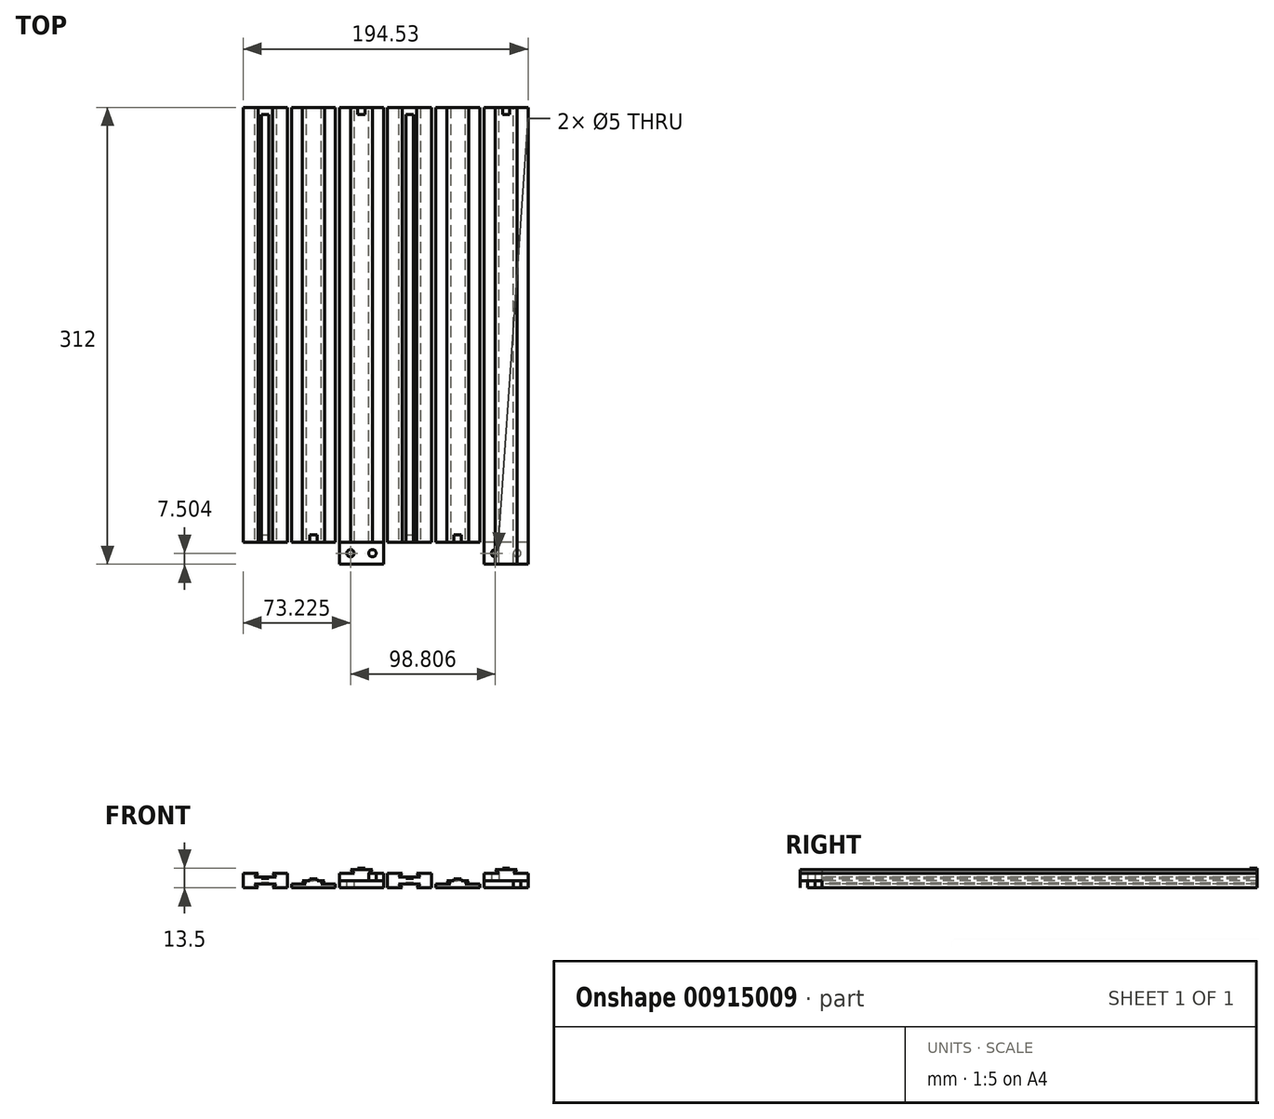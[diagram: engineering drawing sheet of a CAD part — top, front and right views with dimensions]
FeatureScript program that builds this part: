
annotation { "Feature Type Name" : "Feature", "Feature Type Description" : "" }
export const myFeature = defineFeature(function(context is Context, id is Id, definition is map)
    precondition{}
    {
        {
            var Q0;
            Q0=qCreatedBy(makeId("Top.planeOp"),FACE);
            var sketch = newSketch(context, id + "F0", { "sketchPlane" : qUnion([Q0])});
            skLineSegment(sketch, "E0.bottom", {"start": v(15, 5) * mm, "end": v(-15, 5) * mm});
            skLineSegment(sketch, "E0.top", {"start": v(15, -5) * mm, "end": v(-15, -5) * mm});
            skLineSegment(sketch, "E0.left", {"start": v(15, 5) * mm, "end": v(15, -5) * mm});
            skLineSegment(sketch, "E0.right", {"start": v(-15, 5) * mm, "end": v(-15, -5) * mm});
            skPoint(sketch, "E0.middle", {"position": v(0, 0) * mm});
            skSolve(sketch);
        }
        {
            var Q0;
            Q0 = qSketchRegion(id + "F0", true);
            extrude(context, id + "F1", {"entities" : qUnion([Q0]), "depth" : 297 * mm, "offsetDistance" : 25.4 * mm});
        }
        {
            var Q0;
            Q0=makeQuery(id+"F1.opExtrude","CAP_FACE",FACE,{"disambiguationData":[OSD([sQuery(id+"F0.wireOp",EDGE,"E0.bottom"),sQuery(id+"F0.wireOp",EDGE,"E0.top"),sQuery(id+"F0.wireOp",EDGE,"E0.left"),sQuery(id+"F0.wireOp",EDGE,"E0.right")])],"isStart":false});
            var sketch = newSketch(context, id + "F2", { "sketchPlane" : qUnion([Q0])});
            skLineSegment(sketch, "E1", {"start": v(5, -5) * mm, "end": v(7.5, -2.5) * mm});
            skLineSegment(sketch, "E2", {"start": v(7.5, -2.5) * mm, "end": v(-7.5, -2.5) * mm});
            skLineSegment(sketch, "E3", {"start": v(-7.5, -2.5) * mm, "end": v(-5, -5) * mm});
            skLineSegment(sketch, "E4", {"start": v(-5, -5) * mm, "end": v(5, -5) * mm});
            skLineSegment(sketch, "E5", {"start": v(0, 5) * mm, "end": v(0, -5) * mm, "construction": true});
            skLineSegment(sketch, "E6", {"start": v(0, -5) * mm, "end": v(0, -2.5) * mm, "construction": true});
            skLineSegment(sketch, "E7", {"start": v(7.5, 2.5) * mm, "end": v(-7.5, 2.5) * mm});
            skLineSegment(sketch, "E8.MirrorCS", {"start": v(-5, 5) * mm, "end": v(5, 5) * mm});
            skLineSegment(sketch, "E9.MirrorCS", {"start": v(-7.5, 2.5) * mm, "end": v(-5, 5) * mm});
            skLineSegment(sketch, "E10.MirrorCS", {"start": v(5, 5) * mm, "end": v(7.5, 2.5) * mm});
            skSolve(sketch);
        }
        {
            var Q0;
            Q0=makeQuery(id+"F2.imprint","IMPRINT",FACE,{"disambiguationData":[TD([[makeQuery(id+"F2.imprint","IMPRINT",EDGE,{"derivedFrom":sQuery(id+"F2.wireOp",EDGE,"E7")}),-1.0]])]});
            var Q1;
            Q1=makeQuery(id+"F2.imprint","IMPRINT",FACE,{"disambiguationData":[TD([[makeQuery(id+"F2.imprint","IMPRINT",EDGE,{"derivedFrom":sQuery(id+"F2.wireOp",EDGE,"E1")}),1.0]])]});
            extrude(context, id + "F3", {"entities" : qUnion([Q0, Q1]), "operationType" : NewBodyOperationType.REMOVE, "oppositeDirection" : true, "depth" : 297 * mm, "offsetDistance" : 25.4 * mm});
        }
        {
            var Q0;
            Q0=qCreatedBy(makeId("Top.planeOp"),FACE);
            var sketch = newSketch(context, id + "F4", { "sketchPlane" : qUnion([Q0])});
            skLineSegment(sketch, "E11.bottom", {"start": v(17.89, 5) * mm, "end": v(47.89, 5) * mm});
            skLineSegment(sketch, "E11.top", {"start": v(17.89, 0) * mm, "end": v(47.89, 0) * mm});
            skLineSegment(sketch, "E11.left", {"start": v(17.89, 5) * mm, "end": v(17.89, 0) * mm});
            skLineSegment(sketch, "E11.right", {"start": v(47.89, 5) * mm, "end": v(47.89, 0) * mm});
            skLineSegment(sketch, "E12", {"start": v(0, 0) * mm, "end": v(22.12, 0) * mm, "construction": true});
            skLineSegment(sketch, "E13", {"start": v(32.89, 5) * mm, "end": v(32.89, 0) * mm, "construction": true});
            skLineSegment(sketch, "E14", {"start": v(37.89, 2.5) * mm, "end": v(40.39, 5) * mm});
            skLineSegment(sketch, "E15", {"start": v(40.39, 5) * mm, "end": v(25.39, 5) * mm});
            skLineSegment(sketch, "E16", {"start": v(25.39, 5) * mm, "end": v(27.89, 2.5) * mm});
            skLineSegment(sketch, "E17", {"start": v(27.89, 2.5) * mm, "end": v(37.89, 2.5) * mm});
            skLineSegment(sketch, "E18", {"start": v(32.89, 2.5) * mm, "end": v(32.89, 5) * mm, "construction": true});
            skLineSegment(sketch, "E19", {"start": v(27.89, 2.5) * mm, "end": v(17.89, 2.5) * mm});
            skLineSegment(sketch, "E20", {"start": v(17.89, 2.5) * mm, "end": v(17.89, 5) * mm});
            skLineSegment(sketch, "E21", {"start": v(37.89, 2.5) * mm, "end": v(47.89, 2.5) * mm});
            skLineSegment(sketch, "E22", {"start": v(47.89, 2.5) * mm, "end": v(47.89, 5) * mm});
            skSolve(sketch);
        }
        {
            var Q0;
            Q0=makeQuery(id+"F4.imprint","IMPRINT",FACE,{"disambiguationData":[TD([[makeQuery(id+"F4.imprint","IMPRINT",EDGE,{"derivedFrom":sQuery(id+"F4.wireOp",EDGE,"E14")}),1.0]])]});
            var Q1;
            Q1=makeQuery(id+"F4.imprint","IMPRINT",FACE,{"disambiguationData":[TD([[makeQuery(id+"F4.imprint","IMPRINT",EDGE,{"derivedFrom":sQuery(id+"F4.wireOp",EDGE,"E11.top")}),1.0]])]});
            var Q2;
            {var subQ2=sQuery(id+"F4.wireOp",EDGE,"E16");Q2=makeQuery(id+"F4.imprint","IMPRINT",FACE,{"disambiguationData":[TD([[makeQuery(id+"F4.imprint","IMPRINT",EDGE,{"derivedFrom":subQ2}),-1.0]])]});}
            var Q3;
            {var subQ2=sQuery(id+"F4.wireOp",EDGE,"E14");Q3=makeQuery(id+"F4.imprint","IMPRINT",FACE,{"disambiguationData":[TD([[makeQuery(id+"F4.imprint","IMPRINT",EDGE,{"derivedFrom":subQ2}),-1.0]])]});}
            extrude(context, id + "F5", {"entities" : qUnion([Q0, Q1, Q2, Q3]), "depth" : 297 * mm, "offsetDistance" : 25.4 * mm});
        }
        {
            var Q0;
            Q0=makeQuery(id+"F5.opExtrude","CAP_FACE",FACE,{"disambiguationData":[OSD([sQuery(id+"F4.wireOp",EDGE,"E11.bottom"),sQuery(id+"F4.wireOp",EDGE,"E11.top"),sQuery(id+"F4.wireOp",EDGE,"E11.left"),sQuery(id+"F4.wireOp",EDGE,"E11.right"),sQuery(id+"F4.wireOp",EDGE,"E15"),sQuery(id+"F4.wireOp",EDGE,"E20"),sQuery(id+"F4.wireOp",EDGE,"E22")])],"isStart":false});
            var sketch = newSketch(context, id + "F6", { "sketchPlane" : qUnion([Q0])});
            skLineSegment(sketch, "E23", {"start": v(37.89, 2.5) * mm, "end": v(40.39, 5) * mm});
            skLineSegment(sketch, "E24", {"start": v(40.39, 5) * mm, "end": v(25.39, 5) * mm});
            skLineSegment(sketch, "E25", {"start": v(25.39, 5) * mm, "end": v(27.89, 2.5) * mm});
            skLineSegment(sketch, "E26", {"start": v(27.89, 2.5) * mm, "end": v(37.89, 2.5) * mm});
            skLineSegment(sketch, "E27", {"start": v(32.89, 5) * mm, "end": v(32.89, 0) * mm, "construction": true});
            skLineSegment(sketch, "E28", {"start": v(27.89, 2.5) * mm, "end": v(17.89, 2.5) * mm});
            skLineSegment(sketch, "E29", {"start": v(37.89, 2.5) * mm, "end": v(47.89, 2.5) * mm});
            skSolve(sketch);
        }
        {
            var Q0;
            {var subQ0=sQuery(id+"F6.wireOp",EDGE,"E25");Q0=makeQuery(id+"F6.imprint","IMPRINT",FACE,{"disambiguationData":[TD([[makeQuery(id+"F6.imprint","IMPRINT",EDGE,{"derivedFrom":subQ0}),-1.0]])]});}
            var Q1;
            {var subQ0=sQuery(id+"F6.wireOp",EDGE,"E23");Q1=makeQuery(id+"F6.imprint","IMPRINT",FACE,{"disambiguationData":[TD([[makeQuery(id+"F6.imprint","IMPRINT",EDGE,{"derivedFrom":subQ0}),-1.0]])]});}
            var Q2;
            Q2 = qSketchRegion(id + "F12", true);
            extrude(context, id + "F7", {"entities" : qUnion([Q0, Q1, Q2]), "operationType" : NewBodyOperationType.REMOVE, "oppositeDirection" : true, "depth" : 297 * mm, "offsetDistance" : 25.4 * mm});
        }
        {
            var Q0;
            Q0=makeQuery(id+"F5.opExtrude","SWEPT_FACE",FACE,{"disambiguationData":[OSD([sQuery(id+"F4.wireOp",EDGE,"E11.bottom"),sQuery(id+"F4.wireOp",EDGE,"E15")])]});
            var sketch = newSketch(context, id + "F8", { "sketchPlane" : qUnion([Q0])});
            skLineSegment(sketch, "E30", {"start": v(-32.89, 297) * mm, "end": v(-32.89, 0) * mm, "construction": true});
            skLineSegment(sketch, "E31", {"start": v(-35.39, 297) * mm, "end": v(-35.39, 292) * mm});
            skLineSegment(sketch, "E32", {"start": v(-35.39, 292) * mm, "end": v(-30.39, 292) * mm});
            skLineSegment(sketch, "E33", {"start": v(-30.39, 292) * mm, "end": v(-30.39, 297) * mm});
            skLineSegment(sketch, "E34", {"start": v(-30.39, 297) * mm, "end": v(-35.39, 297) * mm});
            skLineSegment(sketch, "E35", {"start": v(-32.89, 292) * mm, "end": v(-32.89, 297) * mm, "construction": true});
            skSolve(sketch);
        }
        {
            var Q0;
            Q0=makeQuery(id+"F8.imprint","IMPRINT",FACE,{"disambiguationData":[TD([[makeQuery(id+"F8.imprint","IMPRINT",EDGE,{"derivedFrom":sQuery(id+"F8.wireOp",EDGE,"E31")}),1.0]])]});
            extrude(context, id + "F9", {"entities" : qUnion([Q0]), "operationType" : NewBodyOperationType.ADD, "depth" : 1 * mm, "offsetDistance" : 25.4 * mm});
        }
        {
            var Q0;
            Q0=makeQuery(id+"F3.boolean.opBoolean","COPY",FACE,{"derivedFrom":makeQuery(id+"F3.opExtrude","SWEPT_FACE",FACE,{"disambiguationData":[OSD([sQuery(id+"F2.wireOp",EDGE,"E7")])]})});
            var sketch = newSketch(context, id + "F10", { "sketchPlane" : qUnion([Q0])});
            skLineSegment(sketch, "E36", {"start": v(0, 0) * mm, "end": v(0, 297) * mm, "construction": true});
            skLineSegment(sketch, "E37", {"start": v(-2.5, 297) * mm, "end": v(-2.5, 5) * mm});
            skLineSegment(sketch, "E38", {"start": v(-2.5, 5) * mm, "end": v(2.5, 5) * mm});
            skLineSegment(sketch, "E39", {"start": v(2.5, 5) * mm, "end": v(2.5, 297) * mm});
            skLineSegment(sketch, "E40", {"start": v(2.5, 297) * mm, "end": v(-2.5, 297) * mm});
            skLineSegment(sketch, "E41", {"start": v(0, 5) * mm, "end": v(0, 297) * mm, "construction": true});
            skSolve(sketch);
        }
        {
            var Q0;
            Q0=makeQuery(id+"F10.imprint","IMPRINT",FACE,{"disambiguationData":[TD([[makeQuery(id+"F10.imprint","IMPRINT",EDGE,{"derivedFrom":sQuery(id+"F10.wireOp",EDGE,"E37")}),1.0]])]});
            extrude(context, id + "F11", {"entities" : qUnion([Q0]), "operationType" : NewBodyOperationType.REMOVE, "oppositeDirection" : true, "depth" : 1 * mm, "offsetDistance" : 25.4 * mm});
        }
        {
            var Q0;
            Q0=makeQuery(id+"F9.boolean.opBoolean","MERGE",FACE,{"derivedFrom":[makeQuery(id+"F5.opExtrude","CAP_FACE",FACE,{"disambiguationData":[OSD([sQuery(id+"F4.wireOp",EDGE,"E11.bottom"),sQuery(id+"F4.wireOp",EDGE,"E11.top"),sQuery(id+"F4.wireOp",EDGE,"E11.left"),sQuery(id+"F4.wireOp",EDGE,"E11.right"),sQuery(id+"F4.wireOp",EDGE,"E15"),sQuery(id+"F4.wireOp",EDGE,"E20"),sQuery(id+"F4.wireOp",EDGE,"E22")])],"isStart":false}),makeQuery(id+"F9.opExtrude","SWEPT_FACE",FACE,{"disambiguationData":[OSD([sQuery(id+"F8.wireOp",EDGE,"E34")])]})]});
            var sketch = newSketch(context, id + "F12", { "sketchPlane" : qUnion([Q0])});
            skLineSegment(sketch, "E42", {"start": v(50.73, 0) * mm, "end": v(50.73, 2.5) * mm});
            skLineSegment(sketch, "E43", {"start": v(50.73, 2.5) * mm, "end": v(60.73, 2.5) * mm});
            skLineSegment(sketch, "E44", {"start": v(60.73, 2.5) * mm, "end": v(58.23, 5) * mm});
            skLineSegment(sketch, "E45", {"start": v(58.23, 5) * mm, "end": v(63.23, 5) * mm});
            skLineSegment(sketch, "E46", {"start": v(63.23, 5) * mm, "end": v(63.23, 6) * mm});
            skLineSegment(sketch, "E47", {"start": v(63.23, 6) * mm, "end": v(68.23, 6) * mm});
            skLineSegment(sketch, "E48", {"start": v(68.23, 6) * mm, "end": v(68.23, 5) * mm});
            skLineSegment(sketch, "E49", {"start": v(68.23, 5) * mm, "end": v(73.23, 5) * mm});
            skLineSegment(sketch, "E50", {"start": v(73.23, 5) * mm, "end": v(70.73, 2.5) * mm});
            skLineSegment(sketch, "E51", {"start": v(70.73, 2.5) * mm, "end": v(80.73, 2.5) * mm});
            skLineSegment(sketch, "E52", {"start": v(80.73, 2.5) * mm, "end": v(80.73, 0) * mm});
            skLineSegment(sketch, "E53", {"start": v(80.73, 0) * mm, "end": v(50.73, 0) * mm});
            skSolve(sketch);
        }
        {
            var Q0;
            Q0 = qSketchRegion(id + "F12", true);
            extrude(context, id + "F13", {"entities" : qUnion([Q0]), "depth" : 297 * mm, "offsetDistance" : 25.4 * mm});
        }
        {
            var Q0;
            Q0=makeQuery(id+"F13.opExtrude","SWEPT_BODY",BODY,{"disambiguationData":[OSD([sQuery(id+"F12.wireOp",EDGE,"E42"),sQuery(id+"F12.wireOp",EDGE,"E43"),sQuery(id+"F12.wireOp",EDGE,"E44"),sQuery(id+"F12.wireOp",EDGE,"E45"),sQuery(id+"F12.wireOp",EDGE,"E46"),sQuery(id+"F12.wireOp",EDGE,"E47"),sQuery(id+"F12.wireOp",EDGE,"E48"),sQuery(id+"F12.wireOp",EDGE,"E49"),sQuery(id+"F12.wireOp",EDGE,"E50"),sQuery(id+"F12.wireOp",EDGE,"E51"),sQuery(id+"F12.wireOp",EDGE,"E52"),sQuery(id+"F12.wireOp",EDGE,"E53")])]});
            transform(context, id + "F14", {"entities" : qUnion([Q0]), "transformType" : TransformType.TRANSLATION_3D, "dx" : 0 * mm, "dy" : 0 * mm, "dz" : -297 * mm, "makeCopy" : false});
        }
        {
            var Q0;
            Q0=makeQuery(id+"F13.opExtrude","CAP_FACE",FACE,{"disambiguationData":[OSD([sQuery(id+"F12.wireOp",EDGE,"E42"),sQuery(id+"F12.wireOp",EDGE,"E43"),sQuery(id+"F12.wireOp",EDGE,"E44"),sQuery(id+"F12.wireOp",EDGE,"E45"),sQuery(id+"F12.wireOp",EDGE,"E46"),sQuery(id+"F12.wireOp",EDGE,"E47"),sQuery(id+"F12.wireOp",EDGE,"E48"),sQuery(id+"F12.wireOp",EDGE,"E49"),sQuery(id+"F12.wireOp",EDGE,"E50"),sQuery(id+"F12.wireOp",EDGE,"E51"),sQuery(id+"F12.wireOp",EDGE,"E52"),sQuery(id+"F12.wireOp",EDGE,"E53")])],"isStart":false});
            var sketch = newSketch(context, id + "F15", { "sketchPlane" : qUnion([Q0])});
            skLineSegment(sketch, "E54", {"start": v(63.23, 5) * mm, "end": v(68.23, 5) * mm});
            skSolve(sketch);
        }
        {
            var Q0;
            Q0=makeQuery(id+"F15.imprint","IMPRINT",FACE,{"disambiguationData":[TD([[makeQuery(id+"F15.imprint","IMPRINT",EDGE,{"derivedFrom":sQuery(id+"F15.wireOp",EDGE,"E54")}),1.0]])]});
            extrude(context, id + "F16", {"entities" : qUnion([Q0]), "operationType" : NewBodyOperationType.REMOVE, "oppositeDirection" : true, "depth" : 292 * mm, "offsetDistance" : 25.4 * mm});
        }
        {
            var Q0;
            Q0=makeQuery(id+"F13.opExtrude","SWEPT_FACE",FACE,{"disambiguationData":[OSD([sQuery(id+"F12.wireOp",EDGE,"E53")])]});
            var sketch = newSketch(context, id + "F17", { "sketchPlane" : qUnion([Q0])});
            skLineSegment(sketch, "E55", {"start": v(50.73, 297) * mm, "end": v(80.73, 297) * mm});
            skLineSegment(sketch, "E56", {"start": v(80.73, 297) * mm, "end": v(80.73, 0) * mm});
            skLineSegment(sketch, "E57", {"start": v(80.73, 0) * mm, "end": v(50.73, 0) * mm});
            skLineSegment(sketch, "E58", {"start": v(50.73, 0) * mm, "end": v(50.73, 297) * mm});
            skSolve(sketch);
        }
        {
            var Q0;
            Q0=makeQuery(id+"F17.imprint","IMPRINT",FACE,{"disambiguationData":[TD([[makeQuery(id+"F17.imprint","IMPRINT",EDGE,{"derivedFrom":sQuery(id+"F17.wireOp",EDGE,"E55")}),1.0]])]});
            extrude(context, id + "F18", {"entities" : qUnion([Q0]), "operationType" : NewBodyOperationType.ADD, "depth" : 7.5 * mm, "offsetDistance" : 25.4 * mm});
        }
        {
            var Q0;
            Q0=makeQuery(id+"F3.boolean.opBoolean","COPY",FACE,{"derivedFrom":makeQuery(id+"F3.opExtrude","SWEPT_FACE",FACE,{"disambiguationData":[OSD([sQuery(id+"F2.wireOp",EDGE,"E2")])]})});
            var sketch = newSketch(context, id + "F19", { "sketchPlane" : qUnion([Q0])});
            skLineSegment(sketch, "E59", {"start": v(0, 297) * mm, "end": v(0, 0) * mm, "construction": true});
            skLineSegment(sketch, "E60", {"start": v(-2.5, 0) * mm, "end": v(2.5, 0) * mm});
            skLineSegment(sketch, "E61", {"start": v(-2.5, 292) * mm, "end": v(2.5, 292) * mm});
            skLineSegment(sketch, "E62", {"start": v(-2.5, 292) * mm, "end": v(-2.5, 0) * mm});
            skLineSegment(sketch, "E63", {"start": v(2.5, 0) * mm, "end": v(2.5, 292) * mm});
            skLineSegment(sketch, "E64", {"start": v(0, 0) * mm, "end": v(0, 292) * mm, "construction": true});
            skSolve(sketch);
        }
        {
            var Q0;
            Q0=makeQuery(id+"F19.imprint","IMPRINT",FACE,{"disambiguationData":[TD([[makeQuery(id+"F19.imprint","IMPRINT",EDGE,{"derivedFrom":sQuery(id+"F19.wireOp",EDGE,"E60")}),-1.0]])]});
            extrude(context, id + "F20", {"entities" : qUnion([Q0]), "operationType" : NewBodyOperationType.REMOVE, "oppositeDirection" : true, "depth" : 1 * mm, "offsetDistance" : 25.4 * mm});
        }
        {
            var Q0;
            Q0=makeQuery(id+"F18.boolean.opBoolean","MERGE",FACE,{"derivedFrom":[makeQuery(id+"F13.opExtrude","CAP_FACE",FACE,{"disambiguationData":[OSD([sQuery(id+"F12.wireOp",EDGE,"E42"),sQuery(id+"F12.wireOp",EDGE,"E43"),sQuery(id+"F12.wireOp",EDGE,"E44"),sQuery(id+"F12.wireOp",EDGE,"E45"),sQuery(id+"F12.wireOp",EDGE,"E46"),sQuery(id+"F12.wireOp",EDGE,"E47"),sQuery(id+"F12.wireOp",EDGE,"E48"),sQuery(id+"F12.wireOp",EDGE,"E49"),sQuery(id+"F12.wireOp",EDGE,"E50"),sQuery(id+"F12.wireOp",EDGE,"E51"),sQuery(id+"F12.wireOp",EDGE,"E52"),sQuery(id+"F12.wireOp",EDGE,"E53")])],"isStart":false}),makeQuery(id+"F18.opExtrude","SWEPT_FACE",FACE,{"disambiguationData":[OSD([sQuery(id+"F17.wireOp",EDGE,"E55")])]})]});
            var sketch = newSketch(context, id + "F21", { "sketchPlane" : qUnion([Q0])});
            skLineSegment(sketch, "E65", {"start": v(50.73, -2.5) * mm, "end": v(80.73, -2.5) * mm, "construction": true});
            skLineSegment(sketch, "E66", {"start": v(65.73, 5) * mm, "end": v(65.73, -7.5) * mm, "construction": true});
            skLineSegment(sketch, "E67", {"start": v(50.73, -2.5) * mm, "end": v(80.73, -2.5) * mm});
            skLineSegment(sketch, "E68", {"start": v(65.73, 5) * mm, "end": v(65.73, -7.5) * mm});
            skSolve(sketch);
        }
        {
            var Q0;
            {var subQ1=sQuery(id+"F17.wireOp",EDGE,"E55");var subQ4=sQuery(id+"F21.wireOp",EDGE,"E68");var subQ6=makeQuery(id+"F18.opExtrude","CAP_EDGE",EDGE,{"disambiguationData":[OSD([subQ1])],"isStart":false});var subQ8=makeQuery(id+"F21.imprint","INTERSECT",VERTEX,{"derivedFrom":[subQ6,subQ4]});Q0=makeQuery(id+"F21.imprint","IMPRINT",FACE,{"disambiguationData":[TD([[makeQuery(id+"F21.imprint","IMPRINT",EDGE,{"disambiguationData":[TD([[subQ8,1.0]])],"derivedFrom":subQ4}),-1.0]])]});}
            var Q1;
            {var subQ1=sQuery(id+"F17.wireOp",EDGE,"E55");var subQ4=sQuery(id+"F21.wireOp",EDGE,"E68");var subQ6=makeQuery(id+"F18.opExtrude","CAP_EDGE",EDGE,{"disambiguationData":[OSD([subQ1])],"isStart":false});var subQ8=makeQuery(id+"F21.imprint","INTERSECT",VERTEX,{"derivedFrom":[subQ6,subQ4]});Q1=makeQuery(id+"F21.imprint","IMPRINT",FACE,{"disambiguationData":[TD([[makeQuery(id+"F21.imprint","IMPRINT",EDGE,{"disambiguationData":[TD([[subQ8,1.0]])],"derivedFrom":subQ4}),1.0]])]});}
            extrude(context, id + "F22", {"entities" : qUnion([Q0, Q1]), "operationType" : NewBodyOperationType.ADD, "depth" : 15 * mm, "offsetDistance" : 25.4 * mm});
        }
        {
            var Q0;
            Q0=makeQuery(id+"F22.opExtrude","SWEPT_FACE",FACE,{"disambiguationData":[OSD([sQuery(id+"F21.wireOp",EDGE,"E67")])]});
            var sketch = newSketch(context, id + "F23", { "sketchPlane" : qUnion([Q0])});
            skLineSegment(sketch, "E69", {"start": v(-65.73, 312) * mm, "end": v(-65.73, 297) * mm, "construction": true});
            skLineSegment(sketch, "E70", {"start": v(-65.73, 304.5) * mm, "end": v(-80.73, 304.5) * mm, "construction": true});
            skLineSegment(sketch, "E71", {"start": v(-65.73, 304.5) * mm, "end": v(-50.73, 304.5) * mm, "construction": true});
            skLineSegment(sketch, "E72", {"start": v(-73.23, 304.5) * mm, "end": v(-73.23, 297) * mm, "construction": true});
            skLineSegment(sketch, "E73", {"start": v(-58.23, 304.5) * mm, "end": v(-58.23, 297) * mm, "construction": true});
            skCircle(sketch, "E74", {"center": v(-58.23, 304.5) * mm, "radius": 2.5 * mm});
            skCircle(sketch, "E75", {"center": v(-73.23, 304.5) * mm, "radius": 2.5 * mm});
            skSolve(sketch);
        }
        {
            var Q0;
            Q0=makeQuery(id+"F23.imprint","IMPRINT",FACE,{"disambiguationData":[TD([[makeQuery(id+"F23.imprint","IMPRINT",EDGE,{"derivedFrom":sQuery(id+"F23.wireOp",EDGE,"E74")}),1.0]])]});
            extrude(context, id + "F24", {"entities" : qUnion([Q0]), "operationType" : NewBodyOperationType.REMOVE, "endBound" : BoundingType.THROUGH_ALL, "oppositeDirection" : true, "depth" : 25.4 * mm, "offsetDistance" : 25.4 * mm});
        }
        {
            var Q0;
            Q0=makeQuery(id+"F23.imprint","IMPRINT",FACE,{"disambiguationData":[TD([[makeQuery(id+"F23.imprint","IMPRINT",EDGE,{"derivedFrom":sQuery(id+"F23.wireOp",EDGE,"E75")}),1.0]])]});
            extrude(context, id + "F25", {"entities" : qUnion([Q0]), "operationType" : NewBodyOperationType.ADD, "depth" : 5 * mm, "offsetDistance" : 25.4 * mm});
        }
        {
            var Q0;
            Q0=makeQuery(id+"F1.opExtrude","SWEPT_BODY",BODY,{"disambiguationData":[OSD([sQuery(id+"F0.wireOp",EDGE,"E0.bottom"),sQuery(id+"F0.wireOp",EDGE,"E0.top"),sQuery(id+"F0.wireOp",EDGE,"E0.left"),sQuery(id+"F0.wireOp",EDGE,"E0.right")])]});
            var Q1;
            Q1=makeQuery(id+"F5.opExtrude","SWEPT_BODY",BODY,{"disambiguationData":[OSD([sQuery(id+"F4.wireOp",EDGE,"E11.bottom"),sQuery(id+"F4.wireOp",EDGE,"E11.top"),sQuery(id+"F4.wireOp",EDGE,"E11.left"),sQuery(id+"F4.wireOp",EDGE,"E11.right"),sQuery(id+"F4.wireOp",EDGE,"E15"),sQuery(id+"F4.wireOp",EDGE,"E20"),sQuery(id+"F4.wireOp",EDGE,"E22")])]});
            var Q2;
            Q2=makeQuery(id+"F13.opExtrude","SWEPT_BODY",BODY,{"disambiguationData":[OSD([sQuery(id+"F12.wireOp",EDGE,"E42"),sQuery(id+"F12.wireOp",EDGE,"E43"),sQuery(id+"F12.wireOp",EDGE,"E44"),sQuery(id+"F12.wireOp",EDGE,"E45"),sQuery(id+"F12.wireOp",EDGE,"E46"),sQuery(id+"F12.wireOp",EDGE,"E47"),sQuery(id+"F12.wireOp",EDGE,"E48"),sQuery(id+"F12.wireOp",EDGE,"E49"),sQuery(id+"F12.wireOp",EDGE,"E50"),sQuery(id+"F12.wireOp",EDGE,"E51"),sQuery(id+"F12.wireOp",EDGE,"E52"),sQuery(id+"F12.wireOp",EDGE,"E53")])]});
            transform(context, id + "F26", {"entities" : qUnion([Q0, Q1, Q2]), "transformType" : TransformType.TRANSLATION_3D, "dx" : 188.47 * mm, "dy" : 0 * mm, "dz" : 0 * mm, "makeCopy" : true});
        }
        {
            var Q0;
            Q0=makeQuery(id+"F26.opPattern","COPY",BODY,{"derivedFrom":makeQuery(id+"F13.opExtrude","SWEPT_BODY",BODY,{"disambiguationData":[OSD([sQuery(id+"F12.wireOp",EDGE,"E42"),sQuery(id+"F12.wireOp",EDGE,"E43"),sQuery(id+"F12.wireOp",EDGE,"E44"),sQuery(id+"F12.wireOp",EDGE,"E45"),sQuery(id+"F12.wireOp",EDGE,"E46"),sQuery(id+"F12.wireOp",EDGE,"E47"),sQuery(id+"F12.wireOp",EDGE,"E48"),sQuery(id+"F12.wireOp",EDGE,"E49"),sQuery(id+"F12.wireOp",EDGE,"E50"),sQuery(id+"F12.wireOp",EDGE,"E51"),sQuery(id+"F12.wireOp",EDGE,"E52"),sQuery(id+"F12.wireOp",EDGE,"E53")])]}),"instanceName":"1"});
            deleteBodies(context, id + "F27", {"entities" : qUnion([Q0])});
        }
        {
            var Q0;
            Q0=makeQuery(id+"F13.opExtrude","SWEPT_BODY",BODY,{"disambiguationData":[OSD([sQuery(id+"F12.wireOp",EDGE,"E42"),sQuery(id+"F12.wireOp",EDGE,"E43"),sQuery(id+"F12.wireOp",EDGE,"E44"),sQuery(id+"F12.wireOp",EDGE,"E45"),sQuery(id+"F12.wireOp",EDGE,"E46"),sQuery(id+"F12.wireOp",EDGE,"E47"),sQuery(id+"F12.wireOp",EDGE,"E48"),sQuery(id+"F12.wireOp",EDGE,"E49"),sQuery(id+"F12.wireOp",EDGE,"E50"),sQuery(id+"F12.wireOp",EDGE,"E51"),sQuery(id+"F12.wireOp",EDGE,"E52"),sQuery(id+"F12.wireOp",EDGE,"E53")])]});
            transform(context, id + "F28", {"entities" : qUnion([Q0]), "transformType" : TransformType.TRANSLATION_3D, "dx" : 207.26 * mm, "dy" : 0 * mm, "dz" : 0 * mm, "makeCopy" : true});
        }
        {
            var Q0;
            Q0=makeQuery(id+"F28.opPattern","COPY",FACE,{"derivedFrom":makeQuery(id+"F22.opExtrude","SWEPT_FACE",FACE,{"disambiguationData":[OSD([sQuery(id+"F21.wireOp",EDGE,"E67")])]}),"instanceName":"1"});
            var sketch = newSketch(context, id + "F29", { "sketchPlane" : qUnion([Q0])});
            skLineSegment(sketch, "E76", {"start": v(-288, 312) * mm, "end": v(-288, 297) * mm});
            skLineSegment(sketch, "E77", {"start": v(-288, 297) * mm, "end": v(-258, 297) * mm});
            skLineSegment(sketch, "E78", {"start": v(-258, 297) * mm, "end": v(-258, 312) * mm});
            skLineSegment(sketch, "E79", {"start": v(-258, 312) * mm, "end": v(-288, 312) * mm});
            skSolve(sketch);
        }
        {
            var Q0;
            Q0=makeQuery(id+"F28.opPattern","COPY",FACE,{"derivedFrom":makeQuery(id+"F25.opExtrude","CAP_FACE",FACE,{"disambiguationData":[OSD([sQuery(id+"F23.wireOp",EDGE,"E75")])],"isStart":false}),"instanceName":"1"});
            var Q1;
            Q1=makeQuery(id+"F29.imprint","IMPRINT",FACE,{"disambiguationData":[TD([[makeQuery(id+"F29.imprint","IMPRINT",EDGE,{"derivedFrom":sQuery(id+"F29.wireOp",EDGE,"E76")}),1.0]])]});
            extrude(context, id + "F30", {"entities" : qUnion([Q0, Q1]), "operationType" : NewBodyOperationType.REMOVE, "oppositeDirection" : true, "depth" : 25.4 * mm, "offsetDistance" : 25.4 * mm});
        }
        {
            var Q0;
            Q0=makeQuery(id+"F30.boolean.opBoolean","MERGE",FACE,{"derivedFrom":[makeQuery(id+"F28.opPattern","COPY",FACE,{"derivedFrom":makeQuery(id+"F18.boolean.opBoolean","MERGE",FACE,{"derivedFrom":[makeQuery(id+"F13.opExtrude","CAP_FACE",FACE,{"disambiguationData":[OSD([sQuery(id+"F12.wireOp",EDGE,"E42"),sQuery(id+"F12.wireOp",EDGE,"E43"),sQuery(id+"F12.wireOp",EDGE,"E44"),sQuery(id+"F12.wireOp",EDGE,"E45"),sQuery(id+"F12.wireOp",EDGE,"E46"),sQuery(id+"F12.wireOp",EDGE,"E47"),sQuery(id+"F12.wireOp",EDGE,"E48"),sQuery(id+"F12.wireOp",EDGE,"E49"),sQuery(id+"F12.wireOp",EDGE,"E50"),sQuery(id+"F12.wireOp",EDGE,"E51"),sQuery(id+"F12.wireOp",EDGE,"E52"),sQuery(id+"F12.wireOp",EDGE,"E53")])],"isStart":false}),makeQuery(id+"F18.opExtrude","SWEPT_FACE",FACE,{"disambiguationData":[OSD([sQuery(id+"F17.wireOp",EDGE,"E55")])]})]}),"instanceName":"1"})],"fromTools":[makeQuery(id+"F30.opExtrude","SWEPT_FACE",FACE,{"disambiguationData":[OSD([sQuery(id+"F29.wireOp",EDGE,"E77")])]})]});
            var sketch = newSketch(context, id + "F31", { "sketchPlane" : qUnion([Q0])});
            skLineSegment(sketch, "E80", {"start": v(258, -2.5) * mm, "end": v(288, -2.5) * mm});
            skSolve(sketch);
        }
        {
            var Q0;
            {var subQ1=sQuery(id+"F31.wireOp",EDGE,"E80");Q0=makeQuery(id+"F31.imprint","IMPRINT",FACE,{"disambiguationData":[TD([[makeQuery(id+"F31.imprint","IMPRINT",EDGE,{"derivedFrom":subQ1}),1.0]])]});}
            extrude(context, id + "F32", {"entities" : qUnion([Q0]), "operationType" : NewBodyOperationType.ADD, "depth" : 15 * mm, "offsetDistance" : 25.4 * mm});
        }
        {
            var Q0;
            Q0=makeQuery(id+"F32.opExtrude","SWEPT_FACE",FACE,{"disambiguationData":[OSD([sQuery(id+"F31.wireOp",EDGE,"E80")])]});
            var sketch = newSketch(context, id + "F33", { "sketchPlane" : qUnion([Q0])});
            skLineSegment(sketch, "E81", {"start": v(273, 312) * mm, "end": v(273, 297) * mm, "construction": true});
            skLineSegment(sketch, "E82", {"start": v(258, 304.5) * mm, "end": v(273, 304.5) * mm, "construction": true});
            skLineSegment(sketch, "E83", {"start": v(273, 304.5) * mm, "end": v(288, 304.5) * mm, "construction": true});
            skCircle(sketch, "E84", {"center": v(265.5, 304.5) * mm, "radius": 2.5 * mm});
            skCircle(sketch, "E85", {"center": v(280.5, 304.5) * mm, "radius": 2.5 * mm});
            skSolve(sketch);
        }
        {
            var Q0;
            Q0=makeQuery(id+"F33.imprint","IMPRINT",FACE,{"disambiguationData":[TD([[makeQuery(id+"F33.imprint","IMPRINT",EDGE,{"derivedFrom":sQuery(id+"F33.wireOp",EDGE,"E85")}),1.0]])]});
            extrude(context, id + "F34", {"entities" : qUnion([Q0]), "operationType" : NewBodyOperationType.ADD, "depth" : 5 * mm, "offsetDistance" : 25.4 * mm});
        }
        {
            var Q0;
            Q0=makeQuery(id+"F33.imprint","IMPRINT",FACE,{"disambiguationData":[TD([[makeQuery(id+"F33.imprint","IMPRINT",EDGE,{"derivedFrom":sQuery(id+"F33.wireOp",EDGE,"E84")}),1.0]])]});
            extrude(context, id + "F35", {"entities" : qUnion([Q0]), "operationType" : NewBodyOperationType.REMOVE, "oppositeDirection" : true, "depth" : 5 * mm, "offsetDistance" : 25.4 * mm});
        }
        {
            var Q0;
            Q0=makeQuery(id+"F1.opExtrude","SWEPT_BODY",BODY,{"disambiguationData":[OSD([sQuery(id+"F0.wireOp",EDGE,"E0.bottom"),sQuery(id+"F0.wireOp",EDGE,"E0.top"),sQuery(id+"F0.wireOp",EDGE,"E0.left"),sQuery(id+"F0.wireOp",EDGE,"E0.right")])]});
            var Q1;
            Q1=makeQuery(id+"F5.opExtrude","SWEPT_BODY",BODY,{"disambiguationData":[OSD([sQuery(id+"F4.wireOp",EDGE,"E11.bottom"),sQuery(id+"F4.wireOp",EDGE,"E11.top"),sQuery(id+"F4.wireOp",EDGE,"E11.left"),sQuery(id+"F4.wireOp",EDGE,"E11.right"),sQuery(id+"F4.wireOp",EDGE,"E15"),sQuery(id+"F4.wireOp",EDGE,"E20"),sQuery(id+"F4.wireOp",EDGE,"E22")])]});
            var Q2;
            Q2=makeQuery(id+"F13.opExtrude","SWEPT_BODY",BODY,{"disambiguationData":[OSD([sQuery(id+"F12.wireOp",EDGE,"E42"),sQuery(id+"F12.wireOp",EDGE,"E43"),sQuery(id+"F12.wireOp",EDGE,"E44"),sQuery(id+"F12.wireOp",EDGE,"E45"),sQuery(id+"F12.wireOp",EDGE,"E46"),sQuery(id+"F12.wireOp",EDGE,"E47"),sQuery(id+"F12.wireOp",EDGE,"E48"),sQuery(id+"F12.wireOp",EDGE,"E49"),sQuery(id+"F12.wireOp",EDGE,"E50"),sQuery(id+"F12.wireOp",EDGE,"E51"),sQuery(id+"F12.wireOp",EDGE,"E52"),sQuery(id+"F12.wireOp",EDGE,"E53")])]});
            var Q3;
            Q3=makeQuery(id+"F26.opPattern","COPY",BODY,{"derivedFrom":makeQuery(id+"F1.opExtrude","SWEPT_BODY",BODY,{"disambiguationData":[OSD([sQuery(id+"F0.wireOp",EDGE,"E0.bottom"),sQuery(id+"F0.wireOp",EDGE,"E0.top"),sQuery(id+"F0.wireOp",EDGE,"E0.left"),sQuery(id+"F0.wireOp",EDGE,"E0.right")])]}),"instanceName":"1"});
            var Q4;
            Q4=makeQuery(id+"F26.opPattern","COPY",BODY,{"derivedFrom":makeQuery(id+"F5.opExtrude","SWEPT_BODY",BODY,{"disambiguationData":[OSD([sQuery(id+"F4.wireOp",EDGE,"E11.bottom"),sQuery(id+"F4.wireOp",EDGE,"E11.top"),sQuery(id+"F4.wireOp",EDGE,"E11.left"),sQuery(id+"F4.wireOp",EDGE,"E11.right"),sQuery(id+"F4.wireOp",EDGE,"E15"),sQuery(id+"F4.wireOp",EDGE,"E20"),sQuery(id+"F4.wireOp",EDGE,"E22")])]}),"instanceName":"1"});
            var Q5;
            Q5=makeQuery(id+"F28.opPattern","COPY",BODY,{"derivedFrom":makeQuery(id+"F13.opExtrude","SWEPT_BODY",BODY,{"disambiguationData":[OSD([sQuery(id+"F12.wireOp",EDGE,"E42"),sQuery(id+"F12.wireOp",EDGE,"E43"),sQuery(id+"F12.wireOp",EDGE,"E44"),sQuery(id+"F12.wireOp",EDGE,"E45"),sQuery(id+"F12.wireOp",EDGE,"E46"),sQuery(id+"F12.wireOp",EDGE,"E47"),sQuery(id+"F12.wireOp",EDGE,"E48"),sQuery(id+"F12.wireOp",EDGE,"E49"),sQuery(id+"F12.wireOp",EDGE,"E50"),sQuery(id+"F12.wireOp",EDGE,"E51"),sQuery(id+"F12.wireOp",EDGE,"E52"),sQuery(id+"F12.wireOp",EDGE,"E53")])]}),"instanceName":"1"});
            var Q6;
            {var subQ0=sQuery(id+"F0.wireOp",EDGE,"E0.left");var subQ1=sQuery(id+"F0.wireOp",EDGE,"E0.top");Q6=makeQuery(id+"F3.boolean.opBoolean","SPLIT",EDGE,{"disambiguationData":[TD([makeQuery(id+"F1.opExtrude","SWEPT_FACE",FACE,{"disambiguationData":[OSD([subQ0])]})])],"derivedFrom":makeQuery(id+"F1.opExtrude","CAP_EDGE",EDGE,{"disambiguationData":[OSD([subQ1])],"isStart":true})});}
            transform(context, id + "F36", {"entities" : qUnion([Q0, Q1, Q2, Q3, Q4, Q5]), "transformType" : TransformType.ROTATION, "transformAxis" : qUnion([Q6]), "angle" : 270 * degree, "makeCopy" : false});
        }
        {
            var Q0;
            Q0=makeQuery(id+"F28.opPattern","COPY",BODY,{"derivedFrom":makeQuery(id+"F13.opExtrude","SWEPT_BODY",BODY,{"disambiguationData":[OSD([sQuery(id+"F12.wireOp",EDGE,"E42"),sQuery(id+"F12.wireOp",EDGE,"E43"),sQuery(id+"F12.wireOp",EDGE,"E44"),sQuery(id+"F12.wireOp",EDGE,"E45"),sQuery(id+"F12.wireOp",EDGE,"E46"),sQuery(id+"F12.wireOp",EDGE,"E47"),sQuery(id+"F12.wireOp",EDGE,"E48"),sQuery(id+"F12.wireOp",EDGE,"E49"),sQuery(id+"F12.wireOp",EDGE,"E50"),sQuery(id+"F12.wireOp",EDGE,"E51"),sQuery(id+"F12.wireOp",EDGE,"E52"),sQuery(id+"F12.wireOp",EDGE,"E53")])]}),"instanceName":"1"});
            transform(context, id + "F37", {"entities" : qUnion([Q0]), "transformType" : TransformType.TRANSLATION_3D, "dx" : -18.54 * mm, "dy" : 0 * mm, "dz" : 0 * mm, "makeCopy" : false});
        }
        {
            var Q0;
            Q0=makeQuery(id+"F26.opPattern","COPY",BODY,{"derivedFrom":makeQuery(id+"F1.opExtrude","SWEPT_BODY",BODY,{"disambiguationData":[OSD([sQuery(id+"F0.wireOp",EDGE,"E0.bottom"),sQuery(id+"F0.wireOp",EDGE,"E0.top"),sQuery(id+"F0.wireOp",EDGE,"E0.left"),sQuery(id+"F0.wireOp",EDGE,"E0.right")])]}),"instanceName":"1"});
            var Q1;
            Q1=makeQuery(id+"F26.opPattern","COPY",BODY,{"derivedFrom":makeQuery(id+"F5.opExtrude","SWEPT_BODY",BODY,{"disambiguationData":[OSD([sQuery(id+"F4.wireOp",EDGE,"E11.bottom"),sQuery(id+"F4.wireOp",EDGE,"E11.top"),sQuery(id+"F4.wireOp",EDGE,"E11.left"),sQuery(id+"F4.wireOp",EDGE,"E11.right"),sQuery(id+"F4.wireOp",EDGE,"E15"),sQuery(id+"F4.wireOp",EDGE,"E20"),sQuery(id+"F4.wireOp",EDGE,"E22")])]}),"instanceName":"1"});
            var Q2;
            Q2=makeQuery(id+"F28.opPattern","COPY",BODY,{"derivedFrom":makeQuery(id+"F13.opExtrude","SWEPT_BODY",BODY,{"disambiguationData":[OSD([sQuery(id+"F12.wireOp",EDGE,"E42"),sQuery(id+"F12.wireOp",EDGE,"E43"),sQuery(id+"F12.wireOp",EDGE,"E44"),sQuery(id+"F12.wireOp",EDGE,"E45"),sQuery(id+"F12.wireOp",EDGE,"E46"),sQuery(id+"F12.wireOp",EDGE,"E47"),sQuery(id+"F12.wireOp",EDGE,"E48"),sQuery(id+"F12.wireOp",EDGE,"E49"),sQuery(id+"F12.wireOp",EDGE,"E50"),sQuery(id+"F12.wireOp",EDGE,"E51"),sQuery(id+"F12.wireOp",EDGE,"E52"),sQuery(id+"F12.wireOp",EDGE,"E53")])]}),"instanceName":"1"});
            transform(context, id + "F38", {"entities" : qUnion([Q0, Q1, Q2]), "transformType" : TransformType.TRANSLATION_3D, "dx" : -89.92 * mm, "dy" : 0 * mm, "dz" : 0 * mm, "makeCopy" : false});
        }
        {
            var Q0;
            Q0=makeQuery(id+"F5.opExtrude","SWEPT_BODY",BODY,{"disambiguationData":[OSD([sQuery(id+"F4.wireOp",EDGE,"E11.bottom"),sQuery(id+"F4.wireOp",EDGE,"E11.top"),sQuery(id+"F4.wireOp",EDGE,"E11.left"),sQuery(id+"F4.wireOp",EDGE,"E11.right"),sQuery(id+"F4.wireOp",EDGE,"E15"),sQuery(id+"F4.wireOp",EDGE,"E20"),sQuery(id+"F4.wireOp",EDGE,"E22")])]});
            var Q1;
            Q1=makeQuery(id+"F26.opPattern","COPY",BODY,{"derivedFrom":makeQuery(id+"F5.opExtrude","SWEPT_BODY",BODY,{"disambiguationData":[OSD([sQuery(id+"F4.wireOp",EDGE,"E11.bottom"),sQuery(id+"F4.wireOp",EDGE,"E11.top"),sQuery(id+"F4.wireOp",EDGE,"E11.left"),sQuery(id+"F4.wireOp",EDGE,"E11.right"),sQuery(id+"F4.wireOp",EDGE,"E15"),sQuery(id+"F4.wireOp",EDGE,"E20"),sQuery(id+"F4.wireOp",EDGE,"E22")])]}),"instanceName":"1"});
            transform(context, id + "F39", {"entities" : qUnion([Q0, Q1]), "transformType" : TransformType.TRANSLATION_3D, "dx" : 0 * mm, "dy" : 0 * mm, "dz" : -5 * mm, "makeCopy" : false});
        }
        {
            var Q0;
            Q0=makeQuery(id+"F13.opExtrude","SWEPT_BODY",BODY,{"disambiguationData":[OSD([sQuery(id+"F12.wireOp",EDGE,"E42"),sQuery(id+"F12.wireOp",EDGE,"E43"),sQuery(id+"F12.wireOp",EDGE,"E44"),sQuery(id+"F12.wireOp",EDGE,"E45"),sQuery(id+"F12.wireOp",EDGE,"E46"),sQuery(id+"F12.wireOp",EDGE,"E47"),sQuery(id+"F12.wireOp",EDGE,"E48"),sQuery(id+"F12.wireOp",EDGE,"E49"),sQuery(id+"F12.wireOp",EDGE,"E50"),sQuery(id+"F12.wireOp",EDGE,"E51"),sQuery(id+"F12.wireOp",EDGE,"E52"),sQuery(id+"F12.wireOp",EDGE,"E53")])]});
            var Q1;
            Q1=makeQuery(id+"F28.opPattern","COPY",BODY,{"derivedFrom":makeQuery(id+"F13.opExtrude","SWEPT_BODY",BODY,{"disambiguationData":[OSD([sQuery(id+"F12.wireOp",EDGE,"E42"),sQuery(id+"F12.wireOp",EDGE,"E43"),sQuery(id+"F12.wireOp",EDGE,"E44"),sQuery(id+"F12.wireOp",EDGE,"E45"),sQuery(id+"F12.wireOp",EDGE,"E46"),sQuery(id+"F12.wireOp",EDGE,"E47"),sQuery(id+"F12.wireOp",EDGE,"E48"),sQuery(id+"F12.wireOp",EDGE,"E49"),sQuery(id+"F12.wireOp",EDGE,"E50"),sQuery(id+"F12.wireOp",EDGE,"E51"),sQuery(id+"F12.wireOp",EDGE,"E52"),sQuery(id+"F12.wireOp",EDGE,"E53")])]}),"instanceName":"1"});
            transform(context, id + "F40", {"entities" : qUnion([Q0, Q1]), "transformType" : TransformType.TRANSLATION_3D, "dx" : 0 * mm, "dy" : 0 * mm, "dz" : 2.5 * mm, "makeCopy" : false});
        }
        {
            var Q0;
            Q0=makeQuery(id+"F1.opExtrude","SWEPT_BODY",BODY,{"disambiguationData":[OSD([sQuery(id+"F0.wireOp",EDGE,"E0.bottom"),sQuery(id+"F0.wireOp",EDGE,"E0.top"),sQuery(id+"F0.wireOp",EDGE,"E0.left"),sQuery(id+"F0.wireOp",EDGE,"E0.right")])]});
            var Q1;
            Q1=makeQuery(id+"F5.opExtrude","SWEPT_BODY",BODY,{"disambiguationData":[OSD([sQuery(id+"F4.wireOp",EDGE,"E11.bottom"),sQuery(id+"F4.wireOp",EDGE,"E11.top"),sQuery(id+"F4.wireOp",EDGE,"E11.left"),sQuery(id+"F4.wireOp",EDGE,"E11.right"),sQuery(id+"F4.wireOp",EDGE,"E15"),sQuery(id+"F4.wireOp",EDGE,"E20"),sQuery(id+"F4.wireOp",EDGE,"E22")])]});
            var Q2;
            Q2=makeQuery(id+"F13.opExtrude","SWEPT_BODY",BODY,{"disambiguationData":[OSD([sQuery(id+"F12.wireOp",EDGE,"E42"),sQuery(id+"F12.wireOp",EDGE,"E43"),sQuery(id+"F12.wireOp",EDGE,"E44"),sQuery(id+"F12.wireOp",EDGE,"E45"),sQuery(id+"F12.wireOp",EDGE,"E46"),sQuery(id+"F12.wireOp",EDGE,"E47"),sQuery(id+"F12.wireOp",EDGE,"E48"),sQuery(id+"F12.wireOp",EDGE,"E49"),sQuery(id+"F12.wireOp",EDGE,"E50"),sQuery(id+"F12.wireOp",EDGE,"E51"),sQuery(id+"F12.wireOp",EDGE,"E52"),sQuery(id+"F12.wireOp",EDGE,"E53")])]});
            var Q3;
            Q3=makeQuery(id+"F26.opPattern","COPY",BODY,{"derivedFrom":makeQuery(id+"F1.opExtrude","SWEPT_BODY",BODY,{"disambiguationData":[OSD([sQuery(id+"F0.wireOp",EDGE,"E0.bottom"),sQuery(id+"F0.wireOp",EDGE,"E0.top"),sQuery(id+"F0.wireOp",EDGE,"E0.left"),sQuery(id+"F0.wireOp",EDGE,"E0.right")])]}),"instanceName":"1"});
            var Q4;
            Q4=makeQuery(id+"F26.opPattern","COPY",BODY,{"derivedFrom":makeQuery(id+"F5.opExtrude","SWEPT_BODY",BODY,{"disambiguationData":[OSD([sQuery(id+"F4.wireOp",EDGE,"E11.bottom"),sQuery(id+"F4.wireOp",EDGE,"E11.top"),sQuery(id+"F4.wireOp",EDGE,"E11.left"),sQuery(id+"F4.wireOp",EDGE,"E11.right"),sQuery(id+"F4.wireOp",EDGE,"E15"),sQuery(id+"F4.wireOp",EDGE,"E20"),sQuery(id+"F4.wireOp",EDGE,"E22")])]}),"instanceName":"1"});
            var Q5;
            Q5=makeQuery(id+"F28.opPattern","COPY",BODY,{"derivedFrom":makeQuery(id+"F13.opExtrude","SWEPT_BODY",BODY,{"disambiguationData":[OSD([sQuery(id+"F12.wireOp",EDGE,"E42"),sQuery(id+"F12.wireOp",EDGE,"E43"),sQuery(id+"F12.wireOp",EDGE,"E44"),sQuery(id+"F12.wireOp",EDGE,"E45"),sQuery(id+"F12.wireOp",EDGE,"E46"),sQuery(id+"F12.wireOp",EDGE,"E47"),sQuery(id+"F12.wireOp",EDGE,"E48"),sQuery(id+"F12.wireOp",EDGE,"E49"),sQuery(id+"F12.wireOp",EDGE,"E50"),sQuery(id+"F12.wireOp",EDGE,"E51"),sQuery(id+"F12.wireOp",EDGE,"E52"),sQuery(id+"F12.wireOp",EDGE,"E53")])]}),"instanceName":"1"});
            transform(context, id + "F41", {"entities" : qUnion([Q0, Q1, Q2, Q3, Q4, Q5]), "transformType" : TransformType.TRANSLATION_3D, "dx" : -79 * mm, "dy" : 162.8 * mm, "dz" : 0 * mm, "makeCopy" : false});
        }
    });
